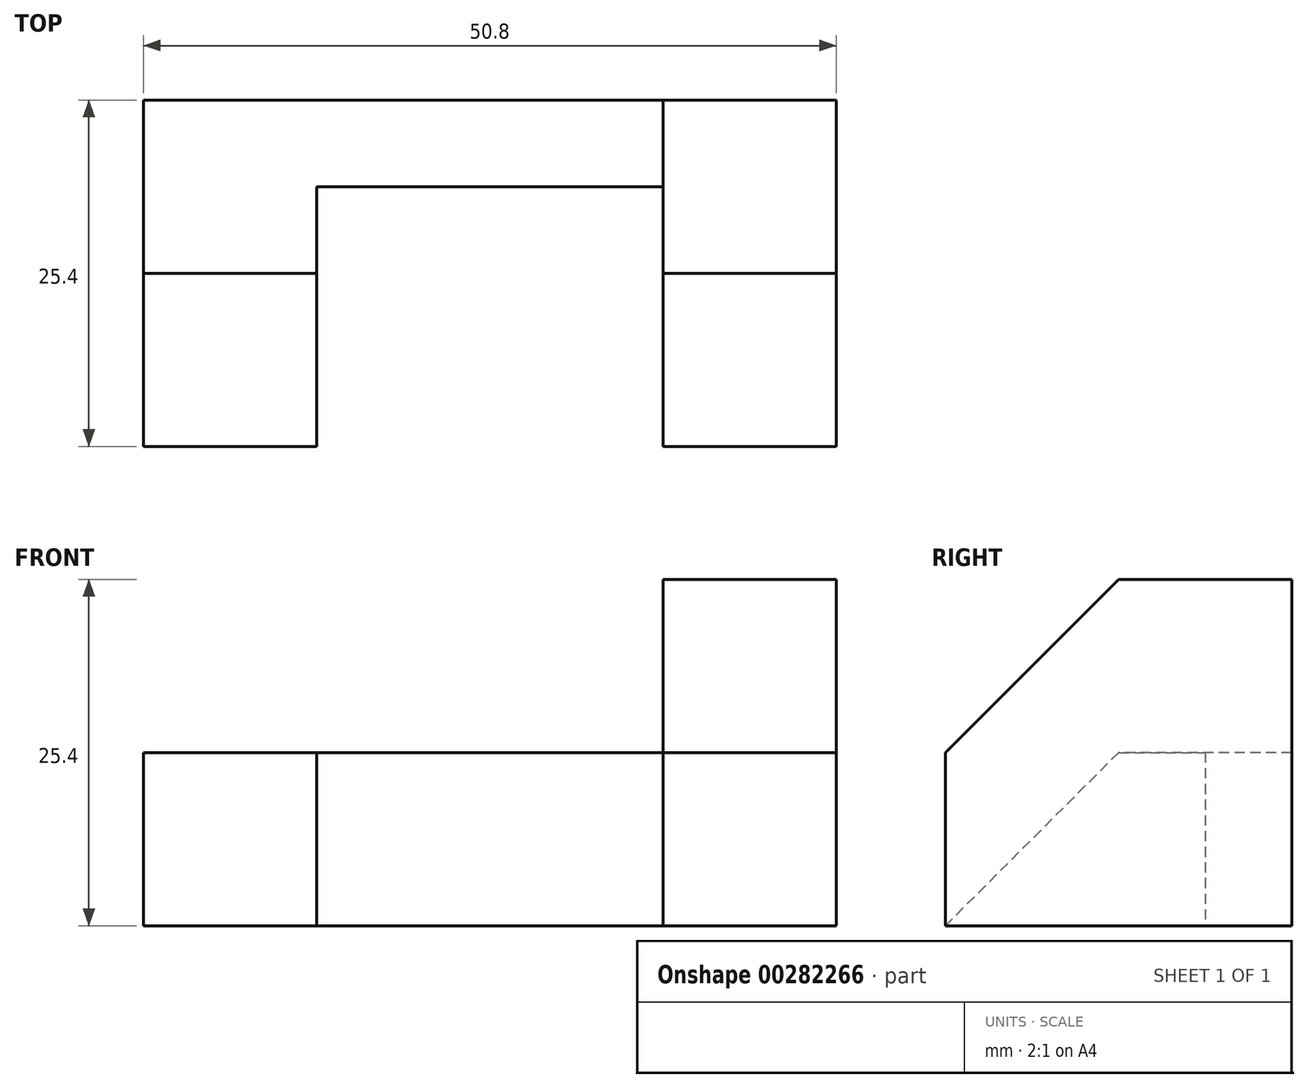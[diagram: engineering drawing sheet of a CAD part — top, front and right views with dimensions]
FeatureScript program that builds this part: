
annotation { "Feature Type Name" : "Feature", "Feature Type Description" : "" }
export const myFeature = defineFeature(function(context is Context, id is Id, definition is map)
    precondition{}
    {
        {
            var Q0;
            Q0=qCreatedBy(makeId("Right.planeOp"),FACE);
            var sketch = newSketch(context, id + "F0", { "sketchPlane" : qUnion([Q0])});
            skLineSegment(sketch, "E0.bottom", {"start": v(0, 0) * mm, "end": v(25.4, 0) * mm});
            skLineSegment(sketch, "E0.top", {"start": v(0, 25.4) * mm, "end": v(25.4, 25.4) * mm});
            skLineSegment(sketch, "E0.left", {"start": v(0, 0) * mm, "end": v(0, 25.4) * mm});
            skLineSegment(sketch, "E0.right", {"start": v(25.4, 0) * mm, "end": v(25.4, 25.4) * mm});
            skSolve(sketch);
        }
        {
            var Q0;
            Q0 = qSketchRegion(id + "F0", true);
            extrude(context, id + "F1", {"entities" : qUnion([Q0]), "depth" : 12.7 * mm});
        }
        {
            var Q0;
            Q0=qCreatedBy(makeId("Right.planeOp"),FACE);
            var sketch = newSketch(context, id + "F2", { "sketchPlane" : qUnion([Q0])});
            skLineSegment(sketch, "E1.bottom", {"start": v(25.4, 0) * mm, "end": v(19.05, 0) * mm});
            skLineSegment(sketch, "E1.top", {"start": v(25.4, 12.7) * mm, "end": v(19.05, 12.7) * mm});
            skLineSegment(sketch, "E1.left", {"start": v(25.4, 0) * mm, "end": v(25.4, 12.7) * mm});
            skLineSegment(sketch, "E1.right", {"start": v(19.05, 0) * mm, "end": v(19.05, 12.7) * mm});
            skSolve(sketch);
        }
        {
            var Q0;
            Q0 = qSketchRegion(id + "F2", true);
            extrude(context, id + "F3", {"entities" : qUnion([Q0]), "operationType" : NewBodyOperationType.ADD, "oppositeDirection" : true, "depth" : 38.1 * mm});
        }
        {
            var Q0;
            Q0=makeQuery(id+"F3.opExtrude","SWEPT_FACE",FACE,{"disambiguationData":[OSD([sQuery(id+"F2.wireOp",EDGE,"E1.right")])]});
            var sketch = newSketch(context, id + "F4", { "sketchPlane" : qUnion([Q0])});
            skLineSegment(sketch, "E2.bottom", {"start": v(-38.1, 12.7) * mm, "end": v(-25.4, 12.7) * mm});
            skLineSegment(sketch, "E2.top", {"start": v(-38.1, 0) * mm, "end": v(-25.4, 0) * mm});
            skLineSegment(sketch, "E2.left", {"start": v(-38.1, 12.7) * mm, "end": v(-38.1, 0) * mm});
            skLineSegment(sketch, "E2.right", {"start": v(-25.4, 12.7) * mm, "end": v(-25.4, 0) * mm});
            skSolve(sketch);
        }
        {
            var Q0;
            Q0 = qSketchRegion(id + "F4", true);
            extrude(context, id + "F5", {"entities" : qUnion([Q0]), "operationType" : NewBodyOperationType.ADD, "depth" : 19.05 * mm});
        }
        {
            var Q0;
            Q0=makeQuery(id+"F1.opExtrude","CAP_FACE",FACE,{"disambiguationData":[OSD([sQuery(id+"F0.wireOp",EDGE,"E0.bottom"),sQuery(id+"F0.wireOp",EDGE,"E0.top"),sQuery(id+"F0.wireOp",EDGE,"E0.left"),sQuery(id+"F0.wireOp",EDGE,"E0.right")])],"isStart":false});
            var sketch = newSketch(context, id + "F6", { "sketchPlane" : qUnion([Q0])});
            skLineSegment(sketch, "E3", {"start": v(0, 25.4) * mm, "end": v(0, 12.7) * mm});
            skLineSegment(sketch, "E4", {"start": v(0, 12.7) * mm, "end": v(12.7, 25.4) * mm});
            skLineSegment(sketch, "E5", {"start": v(12.7, 25.4) * mm, "end": v(0, 25.4) * mm});
            skSolve(sketch);
        }
        {
            var Q0;
            Q0 = qSketchRegion(id + "F6", true);
            extrude(context, id + "F7", {"entities" : qUnion([Q0]), "operationType" : NewBodyOperationType.REMOVE, "oppositeDirection" : true, "depth" : 12.7 * mm});
        }
        {
            var Q0;
            Q0=makeQuery(id+"F5.opExtrude","SWEPT_FACE",FACE,{"disambiguationData":[OSD([sQuery(id+"F4.wireOp",EDGE,"E2.right")])]});
            var sketch = newSketch(context, id + "F8", { "sketchPlane" : qUnion([Q0])});
            skLineSegment(sketch, "E6", {"start": v(0, 12.7) * mm, "end": v(12.7, 12.7) * mm});
            skLineSegment(sketch, "E7", {"start": v(12.7, 12.7) * mm, "end": v(0, 0) * mm});
            skLineSegment(sketch, "E8", {"start": v(0, 0) * mm, "end": v(0, 12.7) * mm});
            skSolve(sketch);
        }
        {
            var Q0;
            Q0 = qSketchRegion(id + "F8", true);
            extrude(context, id + "F9", {"entities" : qUnion([Q0]), "operationType" : NewBodyOperationType.REMOVE, "oppositeDirection" : true, "depth" : 12.7 * mm});
        }
    });
